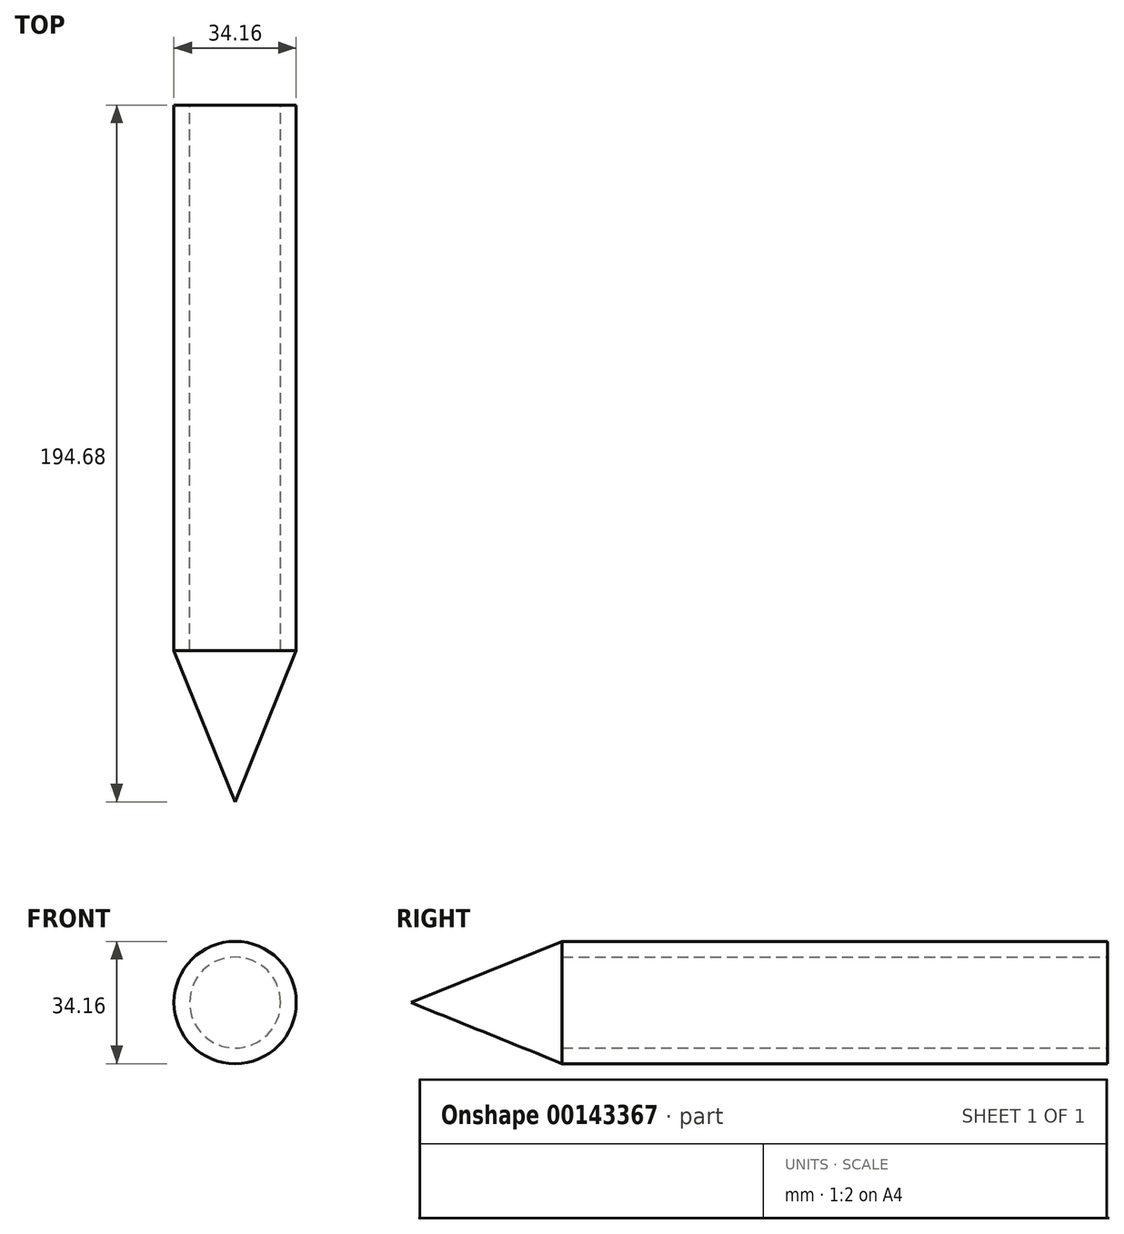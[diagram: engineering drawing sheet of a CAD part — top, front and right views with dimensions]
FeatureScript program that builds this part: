
annotation { "Feature Type Name" : "Feature", "Feature Type Description" : "" }
export const myFeature = defineFeature(function(context is Context, id is Id, definition is map)
    precondition{}
    {
        {
            var Q0;
            Q0=qCreatedBy(makeId("Front.planeOp"),FACE);
            var sketch = newSketch(context, id + "F0", { "sketchPlane" : qUnion([Q0])});
            skCircle(sketch, "E0", {"center": v(0, 0) * mm, "radius": 12.7 * mm});
            skCircle(sketch, "E1", {"center": v(0, 0) * mm, "radius": 17.08 * mm});
            skSolve(sketch);
        }
        {
            var Q0;
            Q0 = qSketchRegion(id + "F0", true);
            extrude(context, id + "F1", {"entities" : qUnion([Q0]), "depth" : 152.4 * mm});
        }
        {
            var Q0;
            Q0=makeQuery(id+"F1.opExtrude","CAP_FACE",FACE,{"disambiguationData":[OSD([sQuery(id+"F0.wireOp",EDGE,"E0"),sQuery(id+"F0.wireOp",EDGE,"E1")])],"isStart":false});
            var sketch = newSketch(context, id + "F2", { "sketchPlane" : qUnion([Q0])});
            skCircle(sketch, "E2.0", {"center": v(0, 0) * mm, "radius": 17.08 * mm});
            skSolve(sketch);
        }
        {
            var Q0;
            Q0 = qSketchRegion(id + "F2", true);
            extrude(context, id + "F3", {"entities" : qUnion([Q0]), "operationType" : NewBodyOperationType.ADD, "depth" : 50.8 * mm, "hasDraft" : true, "draftAngle" : 22 * degree, "draftPullDirection" : true});
        }
    });
